# Revit family: 205_SIBOL-100-_-1200
name_source: partatom
category: Duct Accessories
units: mm (PartAtom-declared; Revit-internal decimal feet)

## family parameters
Always vertical = Yes
Cut with Voids When Loaded = No
Part Type = Breaks Into
Round Connector Dimension = Use Diameter
Shared = No
Work Plane-Based = No

## types (17) — shared parameters
Description = CIRCULAR SILENCER WITH CORE
L1 = 8 mm  [stored 0.0262467 ft]
L2 = 1184 mm
L2D = 1200 mm
LL = 600 mm  [stored 1.9685 ft]
Manufacturer = Alnor
QmdConnectorList = 201;D;202;D
URL = http://www.ventilation-alnor.co.uk
magiPartTypeId = 205
magiProductFamilyId = SIBOL-100-*-1200

## per-type parameters (varying)
| type | CD1 | CD2 | D | H2D | R | W2D |
| SIBOL-100-200-1200 | 200 mm  [stored 0.656168 ft] | 201 mm  [stored 0.659449 ft] | 200 mm | 400 mm  [stored 1.31234 ft] | 100 mm  [stored 0.328084 ft] | 400 mm  [stored 1.31234 ft] |
| SIBOL-100-1000-1200 | 625 mm | 626 mm | 1000 mm | 1200 mm | 500 mm | 1200 mm |
| SIBOL-100-900-1200 | 625 mm | 626 mm | 900 mm | 1100 mm | 450 mm | 1100 mm |
| SIBOL-100-800-1200 | 560 mm | 561 mm | 800 mm | 1000 mm | 400 mm  [stored 1.31234 ft] | 1000 mm |
| SIBOL-100-710-1200 | 450 mm | 451 mm | 710 mm | 910 mm | 355 mm | 910 mm |
| SIBOL-100-630-1200 | 400 mm  [stored 1.31234 ft] | 401 mm | 630 mm | 830 mm | 315 mm | 830 mm |
| SIBOL-100-600-1200 | 400 mm  [stored 1.31234 ft] | 401 mm | 600 mm | 800 mm | 300 mm  [stored 0.984252 ft] | 800 mm |
| SIBOL-100-560-1200 | 400 mm  [stored 1.31234 ft] | 401 mm | 560 mm | 760 mm | 280 mm | 760 mm |
| SIBOL-100-500-1200 | 355 mm | 356 mm | 500 mm | 700 mm | 250 mm | 700 mm |
| SIBOL-100-450-1200 | 315 mm | 316 mm | 450 mm | 650 mm | 225 mm | 650 mm |
| SIBOL-100-400-1200 | 300 mm  [stored 0.984252 ft] | 301 mm  [stored 0.987533 ft] | 400 mm | 600 mm  [stored 1.9685 ft] | 200 mm  [stored 0.656168 ft] | 600 mm  [stored 1.9685 ft] |
| SIBOL-100-355-1200 | 280 mm | 281 mm | 355 mm | 555 mm | 178 mm | 555 mm |
| SIBOL-100-315-1200 | 250 mm | 251 mm | 315 mm | 515 mm | 158 mm | 515 mm |
| SIBOL-100-300-1200 | 250 mm | 251 mm | 300 mm | 500 mm | 150 mm | 500 mm |
| SIBOL-100-280-1200 | 250 mm | 251 mm | 280 mm | 480 mm | 140 mm | 480 mm |
| SIBOL-100-250-1200 | 225 mm | 226 mm | 250 mm | 450 mm | 125 mm | 450 mm |
| SIBOL-100-224-1200 | 225 mm | 226 mm | 224 mm | 424 mm | 112 mm | 424 mm |

note: column(s) folded — value = type name in every type: MC Product Code, magiProductId

note: [stored X ft] marks values corroborated as IEEE doubles in the binary element streams (Revit-internal decimal feet)

## geometry (parser evidence)
native form markers: Blend x4, Sweep x1
no freeform markers — native parametric forms only
